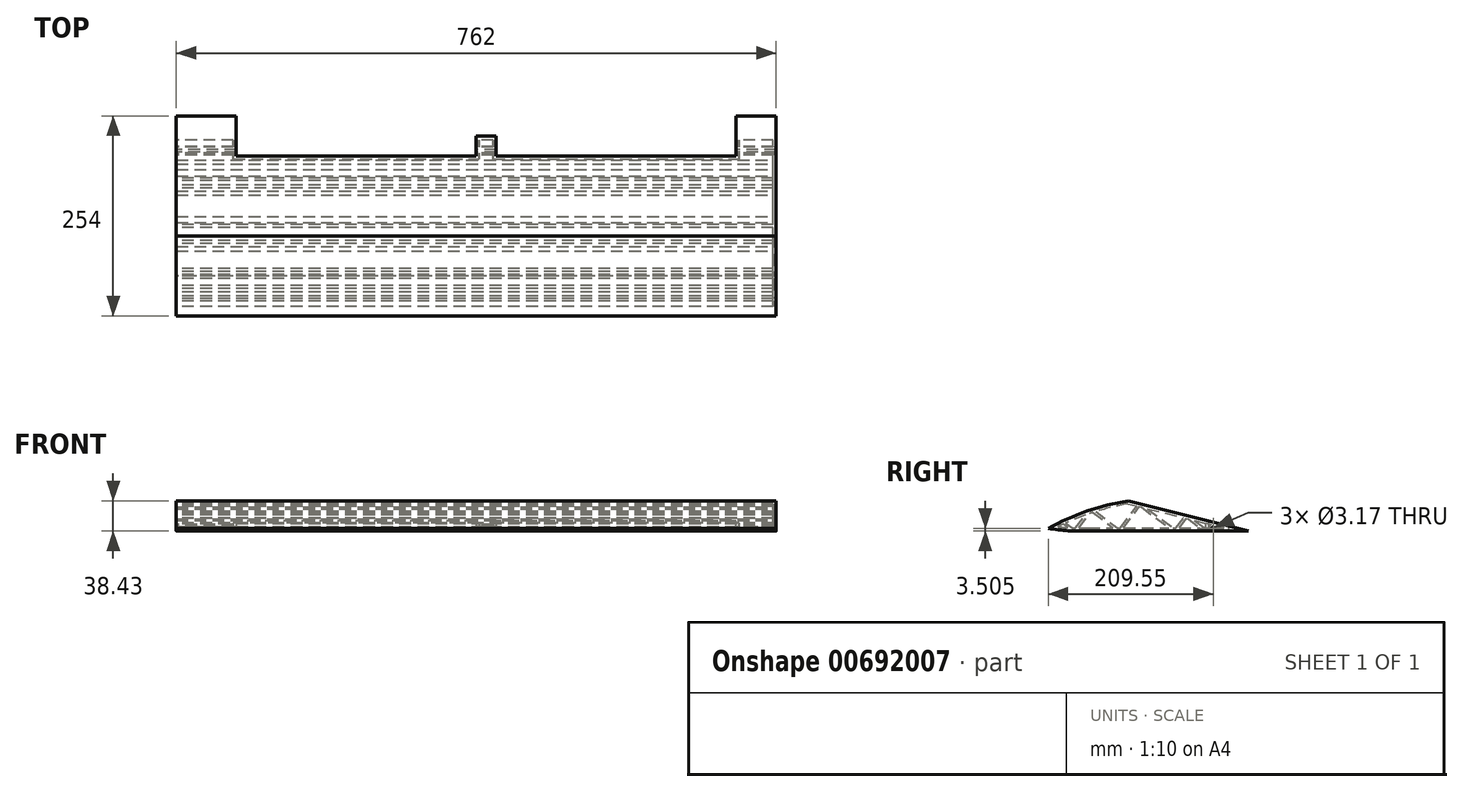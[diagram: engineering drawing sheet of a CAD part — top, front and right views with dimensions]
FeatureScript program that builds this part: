
annotation { "Feature Type Name" : "Feature", "Feature Type Description" : "" }
export const myFeature = defineFeature(function(context is Context, id is Id, definition is map)
    precondition{}
    {
        {
            var Q0;
            Q0=qCreatedBy(makeId("Right.planeOp"),FACE);
            var sketch = newSketch(context, id + "F0", { "sketchPlane" : qUnion([Q0])});
            skLineSegment(sketch, "E0.bottom", {"start": v(-127, 19.05) * mm, "end": v(127, 19.05) * mm});
            skLineSegment(sketch, "E0.top", {"start": v(-127, -19.05) * mm, "end": v(-120.65, -19.05) * mm});
            skLineSegment(sketch, "E0.left", {"start": v(-127, 19.05) * mm, "end": v(-127, -19.05) * mm});
            skLineSegment(sketch, "E0.right", {"start": v(127, 19.05) * mm, "end": v(127, -19.05) * mm});
            skPoint(sketch, "E0.middle", {"position": v(0, 0) * mm});
            skLineSegment(sketch, "E1", {"start": v(-123.83, -17.46) * mm, "end": v(-127, -15.88) * mm});
            skLineSegment(sketch, "E2", {"start": v(-127, 19.05) * mm, "end": v(-76.2, 19.05) * mm});
            skLineSegment(sketch, "E3", {"start": v(-76.2, 19.05) * mm, "end": v(-76.2, 6.35) * mm});
            skLineSegment(sketch, "E4", {"start": v(-127, 19.05) * mm, "end": v(-25.4, 19.05) * mm});
            skLineSegment(sketch, "E5", {"start": v(-25.4, 19.05) * mm, "end": v(127, -19.05) * mm});
            skLineSegment(sketch, "E6", {"start": v(-76.2, 6.35) * mm, "end": v(-76.2, -19.05) * mm});
            skArc(sketch, "E7", {"start": v(-127, -15.88) * mm, "mid": v(-101.7, -18.95) * mm, "end": v(-76.2, -19.05) * mm});
            skLineSegment(sketch, "E8.trimOffspring", {"start": v(-76.2, -19.05) * mm, "end": v(127, -19.05) * mm});
            skPoint(sketch, "E9.orphan", {"position": v(-123.83, -17.46) * mm});
            skPoint(sketch, "E10.orphan", {"position": v(-76.2, -17.46) * mm});
            skPoint(sketch, "E11.end.orphan", {"position": v(-100.01, -17.46) * mm});
            skArc(sketch, "E12", {"start": v(-25.4, 19.05) * mm, "mid": v(-77.67, 5.85) * mm, "end": v(-127, -15.88) * mm});
            skLineSegment(sketch, "E13", {"start": v(127, -19.05) * mm, "end": v(101.6, -19.05) * mm});
            skLineSegment(sketch, "E14", {"start": v(101.6, -19.05) * mm, "end": v(76.2, -19.05) * mm});
            skLineSegment(sketch, "E15", {"start": v(76.2, -19.05) * mm, "end": v(50.8, 0) * mm});
            skLineSegment(sketch, "E16", {"start": v(50.8, 0) * mm, "end": v(36.51, -19.05) * mm});
            skLineSegment(sketch, "E17", {"start": v(36.51, -19.05) * mm, "end": v(-8.73, 14.88) * mm});
            skLineSegment(sketch, "E18", {"start": v(-8.73, 14.88) * mm, "end": v(-34.18, -19.05) * mm});
            skLineSegment(sketch, "E19", {"start": v(-34.18, -19.05) * mm, "end": v(-70.53, 8.21) * mm});
            skLineSegment(sketch, "E20", {"start": v(-70.53, 8.21) * mm, "end": v(-91.2, -19.35) * mm});
            skLineSegment(sketch, "E21", {"start": v(-91.2, -19.35) * mm, "end": v(-108.35, -6.5) * mm});
            skLineSegment(sketch, "E22", {"start": v(76.2, -19.05) * mm, "end": v(74.3, -21.6) * mm});
            skLineSegment(sketch, "E23", {"start": v(74.3, -21.6) * mm, "end": v(48.9, -2.54) * mm});
            skLineSegment(sketch, "E24", {"start": v(48.9, -2.54) * mm, "end": v(46.36, -0.64) * mm});
            skLineSegment(sketch, "E25", {"start": v(46.36, -0.64) * mm, "end": v(33.97, -17.14) * mm});
            skLineSegment(sketch, "E26", {"start": v(33.97, -17.14) * mm, "end": v(32.07, -19.68) * mm});
            skLineSegment(sketch, "E27", {"start": v(32.07, -19.68) * mm, "end": v(-10.64, 12.34) * mm});
            skLineSegment(sketch, "E28", {"start": v(-10.64, 12.34) * mm, "end": v(-13.18, 14.25) * mm});
            skLineSegment(sketch, "E29", {"start": v(-13.18, 14.25) * mm, "end": v(-36.72, -17.14) * mm});
            skLineSegment(sketch, "E30", {"start": v(-36.72, -17.14) * mm, "end": v(-38.63, -19.68) * mm});
            skLineSegment(sketch, "E31", {"start": v(-38.63, -19.68) * mm, "end": v(-72.43, 5.67) * mm});
            skLineSegment(sketch, "E32", {"start": v(-72.43, 5.67) * mm, "end": v(-74.97, 7.58) * mm});
            skLineSegment(sketch, "E33", {"start": v(-74.97, 7.58) * mm, "end": v(-93.74, -17.45) * mm});
            skLineSegment(sketch, "E34", {"start": v(-93.74, -17.45) * mm, "end": v(-95.65, -19.99) * mm});
            skLineSegment(sketch, "E35", {"start": v(-95.65, -19.99) * mm, "end": v(-111.6, -8.02) * mm});
            skLineSegment(sketch, "E36", {"start": v(127, -19.05) * mm, "end": v(82.55, -19.05) * mm});
            skLineSegment(sketch, "E37", {"start": v(82.55, -19.05) * mm, "end": v(82.55, -15.88) * mm});
            skCircle(sketch, "E38", {"center": v(82.55, -15.88) * mm, "radius": 1.59 * mm});
            skSolve(sketch);
        }
        {
            var Q0;
            {var subQ0=sQuery(id+"F0.wireOp",EDGE,"E1");Q0=makeQuery(id+"F0.imprint","IMPRINT",FACE,{"disambiguationData":[TD([[makeQuery(id+"F0.imprint","IMPRINT",EDGE,{"derivedFrom":subQ0}),-1.0]])]});}
            var Q1;
            {var subQ0=sQuery(id+"F0.wireOp",EDGE,"E5");Q1=makeQuery(id+"F0.imprint","IMPRINT",FACE,{"disambiguationData":[TD([[makeQuery(id+"F0.imprint","IMPRINT",EDGE,{"derivedFrom":subQ0}),-1.0]])]});}
            var Q2;
            {var subQ0=sQuery(id+"F0.wireOp",EDGE,"E15");Q2=makeQuery(id+"F0.imprint","IMPRINT",FACE,{"disambiguationData":[TD([[makeQuery(id+"F0.imprint","IMPRINT",EDGE,{"derivedFrom":subQ0}),1.0]])]});}
            var Q3;
            {var subQ0=sQuery(id+"F0.wireOp",EDGE,"E23");var subQ1=sQuery(id+"F0.wireOp",EDGE,"E8.trimOffspring");var subQ2=makeQuery(id+"F0.imprint","INTERSECT",VERTEX,{"derivedFrom":[subQ1,subQ0]});Q3=makeQuery(id+"F0.imprint","IMPRINT",FACE,{"disambiguationData":[TD([[makeQuery(id+"F0.imprint","IMPRINT",EDGE,{"disambiguationData":[TD([[subQ2,1.0]])],"derivedFrom":subQ1}),1.0]])]});}
            var Q4;
            {var subQ0=sQuery(id+"F0.wireOp",EDGE,"E24");Q4=makeQuery(id+"F0.imprint","IMPRINT",FACE,{"disambiguationData":[TD([[makeQuery(id+"F0.imprint","IMPRINT",EDGE,{"derivedFrom":subQ0}),1.0]])]});}
            var Q5;
            {var subQ4=sQuery(id+"F0.wireOp",EDGE,"E24");Q5=makeQuery(id+"F0.imprint","IMPRINT",FACE,{"disambiguationData":[TD([[makeQuery(id+"F0.imprint","IMPRINT",EDGE,{"derivedFrom":subQ4}),-1.0]])]});}
            var Q6;
            {var subQ1=sQuery(id+"F0.wireOp",EDGE,"E8.trimOffspring");var subQ3=sQuery(id+"F0.wireOp",EDGE,"E27");var subQ4=makeQuery(id+"F0.imprint","INTERSECT",VERTEX,{"derivedFrom":[subQ1,subQ3]});Q6=makeQuery(id+"F0.imprint","IMPRINT",FACE,{"disambiguationData":[TD([[makeQuery(id+"F0.imprint","IMPRINT",EDGE,{"disambiguationData":[TD([[subQ4,1.0]])],"derivedFrom":subQ1}),1.0]])]});}
            var Q7;
            {var subQ8=sQuery(id+"F0.wireOp",EDGE,"E28");Q7=makeQuery(id+"F0.imprint","IMPRINT",FACE,{"disambiguationData":[TD([[makeQuery(id+"F0.imprint","IMPRINT",EDGE,{"derivedFrom":subQ8}),-1.0]])]});}
            var Q8;
            {var subQ0=sQuery(id+"F0.wireOp",EDGE,"E20");var subQ1=sQuery(id+"F0.wireOp",EDGE,"E6");var subQ2=makeQuery(id+"F0.imprint","INTERSECT",VERTEX,{"derivedFrom":[subQ1,subQ0]});Q8=makeQuery(id+"F0.imprint","IMPRINT",FACE,{"disambiguationData":[TD([[makeQuery(id+"F0.imprint","IMPRINT",EDGE,{"disambiguationData":[TD([[subQ2,-1.0]])],"derivedFrom":subQ1}),1.0]])]});}
            var Q9;
            {var subQ1=sQuery(id+"F0.wireOp",EDGE,"E6");var subQ3=sQuery(id+"F0.wireOp",EDGE,"E33");var subQ4=makeQuery(id+"F0.imprint","INTERSECT",VERTEX,{"derivedFrom":[subQ1,subQ3]});Q9=makeQuery(id+"F0.imprint","IMPRINT",FACE,{"disambiguationData":[TD([[makeQuery(id+"F0.imprint","IMPRINT",EDGE,{"disambiguationData":[TD([[subQ4,1.0]])],"derivedFrom":subQ1}),-1.0]])]});}
            var Q10;
            {var subQ3=sQuery(id+"F0.wireOp",EDGE,"E7");var subQ7=sQuery(id+"F0.wireOp",EDGE,"E35");var subQ9=makeQuery(id+"F0.imprint","INTERSECT",VERTEX,{"derivedFrom":[subQ3,subQ7]});Q10=makeQuery(id+"F0.imprint","IMPRINT",FACE,{"disambiguationData":[TD([[makeQuery(id+"F0.imprint","IMPRINT",EDGE,{"disambiguationData":[TD([[subQ9,-1.0]])],"derivedFrom":subQ3}),1.0]])]});}
            var Q11;
            {var subQ0=sQuery(id+"F0.wireOp",EDGE,"E20");var subQ1=sQuery(id+"F0.wireOp",EDGE,"E6");var subQ2=makeQuery(id+"F0.imprint","INTERSECT",VERTEX,{"derivedFrom":[subQ1,subQ0]});Q11=makeQuery(id+"F0.imprint","IMPRINT",FACE,{"disambiguationData":[TD([[makeQuery(id+"F0.imprint","IMPRINT",EDGE,{"disambiguationData":[TD([[subQ2,1.0]])],"derivedFrom":subQ1}),-1.0]])]});}
            var Q12;
            {var subQ0=sQuery(id+"F0.wireOp",EDGE,"E30");var subQ1=sQuery(id+"F0.wireOp",EDGE,"E8.trimOffspring");var subQ2=makeQuery(id+"F0.imprint","INTERSECT",VERTEX,{"derivedFrom":[subQ1,subQ0]});Q12=makeQuery(id+"F0.imprint","IMPRINT",FACE,{"disambiguationData":[TD([[makeQuery(id+"F0.imprint","IMPRINT",EDGE,{"disambiguationData":[TD([[subQ2,1.0]])],"derivedFrom":subQ1}),1.0]])]});}
            var Q13;
            {var subQ1=sQuery(id+"F0.wireOp",EDGE,"E20");var subQ5=sQuery(id+"F0.wireOp",EDGE,"E6");var subQ6=makeQuery(id+"F0.imprint","INTERSECT",VERTEX,{"derivedFrom":[subQ5,subQ1]});Q13=makeQuery(id+"F0.imprint","IMPRINT",FACE,{"disambiguationData":[TD([[makeQuery(id+"F0.imprint","IMPRINT",EDGE,{"disambiguationData":[TD([[subQ6,1.0]])],"derivedFrom":subQ5}),1.0]])]});}
            var Q14;
            {var subQ3=sQuery(id+"F0.wireOp",EDGE,"E28");Q14=makeQuery(id+"F0.imprint","IMPRINT",FACE,{"disambiguationData":[TD([[makeQuery(id+"F0.imprint","IMPRINT",EDGE,{"derivedFrom":subQ3}),1.0]])]});}
            var Q15;
            {var subQ3=sQuery(id+"F0.wireOp",EDGE,"E8.trimOffspring");var subQ7=sQuery(id+"F0.wireOp",EDGE,"E27");var subQ9=makeQuery(id+"F0.imprint","INTERSECT",VERTEX,{"derivedFrom":[subQ3,subQ7]});Q15=makeQuery(id+"F0.imprint","IMPRINT",FACE,{"disambiguationData":[TD([[makeQuery(id+"F0.imprint","IMPRINT",EDGE,{"disambiguationData":[TD([[subQ9,-1.0]])],"derivedFrom":subQ3}),1.0]])]});}
            var Q16;
            {var subQ1=sQuery(id+"F0.wireOp",EDGE,"E8.trimOffspring");var subQ3=sQuery(id+"F0.wireOp",EDGE,"E26");var subQ4=makeQuery(id+"F0.imprint","INTERSECT",VERTEX,{"derivedFrom":[subQ1,subQ3]});Q16=makeQuery(id+"F0.imprint","IMPRINT",FACE,{"disambiguationData":[TD([[makeQuery(id+"F0.imprint","IMPRINT",EDGE,{"disambiguationData":[TD([[subQ4,-1.0]])],"derivedFrom":subQ1}),1.0]])]});}
            var Q17;
            {var subQ1=sQuery(id+"F0.wireOp",EDGE,"E8.trimOffspring");var subQ3=sQuery(id+"F0.wireOp",EDGE,"E30");var subQ4=makeQuery(id+"F0.imprint","INTERSECT",VERTEX,{"derivedFrom":[subQ1,subQ3]});Q17=makeQuery(id+"F0.imprint","IMPRINT",FACE,{"disambiguationData":[TD([[makeQuery(id+"F0.imprint","IMPRINT",EDGE,{"disambiguationData":[TD([[subQ4,-1.0]])],"derivedFrom":subQ1}),1.0]])]});}
            var Q18;
            {var subQ0=sQuery(id+"F0.wireOp",EDGE,"E34");var subQ1=sQuery(id+"F0.wireOp",EDGE,"E7");var subQ2=makeQuery(id+"F0.imprint","INTERSECT",VERTEX,{"derivedFrom":[subQ1,subQ0]});Q18=makeQuery(id+"F0.imprint","IMPRINT",FACE,{"disambiguationData":[TD([[makeQuery(id+"F0.imprint","IMPRINT",EDGE,{"disambiguationData":[TD([[subQ2,-1.0]])],"derivedFrom":subQ1}),1.0]])]});}
            var Q19;
            {var subQ0=sQuery(id+"F0.wireOp",EDGE,"E20");var subQ1=sQuery(id+"F0.wireOp",EDGE,"E6");var subQ2=makeQuery(id+"F0.imprint","INTERSECT",VERTEX,{"derivedFrom":[subQ1,subQ0]});Q19=makeQuery(id+"F0.imprint","IMPRINT",FACE,{"disambiguationData":[TD([[makeQuery(id+"F0.imprint","IMPRINT",EDGE,{"disambiguationData":[TD([[subQ2,-1.0]])],"derivedFrom":subQ1}),-1.0]])]});}
            var Q20;
            {var subQ1=sQuery(id+"F0.wireOp",EDGE,"E12");var subQ3=sQuery(id+"F0.wireOp",EDGE,"E32");var subQ4=makeQuery(id+"F0.imprint","INTERSECT",VERTEX,{"derivedFrom":[subQ1,subQ3]});Q20=makeQuery(id+"F0.imprint","IMPRINT",FACE,{"disambiguationData":[TD([[makeQuery(id+"F0.imprint","IMPRINT",EDGE,{"disambiguationData":[TD([[subQ4,1.0]])],"derivedFrom":subQ1}),1.0]])]});}
            var Q21;
            {var subQ1=sQuery(id+"F0.wireOp",EDGE,"E6");var subQ3=sQuery(id+"F0.wireOp",EDGE,"E33");var subQ4=makeQuery(id+"F0.imprint","INTERSECT",VERTEX,{"derivedFrom":[subQ1,subQ3]});Q21=makeQuery(id+"F0.imprint","IMPRINT",FACE,{"disambiguationData":[TD([[makeQuery(id+"F0.imprint","IMPRINT",EDGE,{"disambiguationData":[TD([[subQ4,1.0]])],"derivedFrom":subQ3}),-1.0]])]});}
            var Q22;
            {var subQ1=sQuery(id+"F0.wireOp",EDGE,"E7");var subQ3=sQuery(id+"F0.wireOp",EDGE,"E35");var subQ4=makeQuery(id+"F0.imprint","INTERSECT",VERTEX,{"derivedFrom":[subQ1,subQ3]});Q22=makeQuery(id+"F0.imprint","IMPRINT",FACE,{"disambiguationData":[TD([[makeQuery(id+"F0.imprint","IMPRINT",EDGE,{"disambiguationData":[TD([[subQ4,-1.0]])],"derivedFrom":subQ3}),1.0]])]});}
            extrude(context, id + "F1", {"entities" : qUnion([Q0, Q1, Q2, Q3, Q4, Q5, Q6, Q7, Q8, Q9, Q10, Q11, Q12, Q13, Q14, Q15, Q16, Q17, Q18, Q19, Q20, Q21, Q22]), "depth" : 762 * mm, "offsetDistance" : 25.4 * mm});
        }
        {
            var Q0;
            Q0=makeQuery(id+"F1.opExtrude","SWEPT_BODY",BODY,{"disambiguationData":[OSD([sQuery(id+"F0.wireOp",EDGE,"E0.top"),sQuery(id+"F0.wireOp",EDGE,"E1"),sQuery(id+"F0.wireOp",EDGE,"54O46Pbj-JXbp-sWDO-WlFE-3hnwlmeF4VM1"),sQuery(id+"F0.wireOp",EDGE,"I7tgXKDc-7YU1-26Oo-DtxB-X4BbDVzCFCnU"),sQuery(id+"F0.wireOp",EDGE,"E5")])]});
            var Q1;
            Q1=qCreatedBy(makeId("Right.planeOp"),FACE);
            mirror(context, id + "F2", {"operationType" : NewBodyOperationType.ADD, "entities" : qUnion([Q0]), "mirrorPlane" : qUnion([Q1])});
        }
        {
            var Q0;
            {var subQ0=sQuery(id+"F0.wireOp",EDGE,"E15");Q0=makeQuery(id+"F0.imprint","IMPRINT",FACE,{"disambiguationData":[TD([[makeQuery(id+"F0.imprint","IMPRINT",EDGE,{"derivedFrom":subQ0}),1.0]])]});}
            var Q1;
            {var subQ0=sQuery(id+"F0.wireOp",EDGE,"E24");Q1=makeQuery(id+"F0.imprint","IMPRINT",FACE,{"disambiguationData":[TD([[makeQuery(id+"F0.imprint","IMPRINT",EDGE,{"derivedFrom":subQ0}),1.0]])]});}
            var Q2;
            {var subQ3=sQuery(id+"F0.wireOp",EDGE,"E8.trimOffspring");var subQ7=sQuery(id+"F0.wireOp",EDGE,"E27");var subQ9=makeQuery(id+"F0.imprint","INTERSECT",VERTEX,{"derivedFrom":[subQ3,subQ7]});Q2=makeQuery(id+"F0.imprint","IMPRINT",FACE,{"disambiguationData":[TD([[makeQuery(id+"F0.imprint","IMPRINT",EDGE,{"disambiguationData":[TD([[subQ9,-1.0]])],"derivedFrom":subQ3}),1.0]])]});}
            var Q3;
            {var subQ3=sQuery(id+"F0.wireOp",EDGE,"E28");Q3=makeQuery(id+"F0.imprint","IMPRINT",FACE,{"disambiguationData":[TD([[makeQuery(id+"F0.imprint","IMPRINT",EDGE,{"derivedFrom":subQ3}),1.0]])]});}
            var Q4;
            {var subQ0=sQuery(id+"F0.wireOp",EDGE,"E30");var subQ1=sQuery(id+"F0.wireOp",EDGE,"E8.trimOffspring");var subQ2=makeQuery(id+"F0.imprint","INTERSECT",VERTEX,{"derivedFrom":[subQ1,subQ0]});Q4=makeQuery(id+"F0.imprint","IMPRINT",FACE,{"disambiguationData":[TD([[makeQuery(id+"F0.imprint","IMPRINT",EDGE,{"disambiguationData":[TD([[subQ2,1.0]])],"derivedFrom":subQ1}),1.0]])]});}
            var Q5;
            {var subQ0=sQuery(id+"F0.wireOp",EDGE,"E20");var subQ1=sQuery(id+"F0.wireOp",EDGE,"E6");var subQ2=makeQuery(id+"F0.imprint","INTERSECT",VERTEX,{"derivedFrom":[subQ1,subQ0]});Q5=makeQuery(id+"F0.imprint","IMPRINT",FACE,{"disambiguationData":[TD([[makeQuery(id+"F0.imprint","IMPRINT",EDGE,{"disambiguationData":[TD([[subQ2,1.0]])],"derivedFrom":subQ1}),-1.0]])]});}
            var Q6;
            {var subQ3=sQuery(id+"F0.wireOp",EDGE,"E7");var subQ7=sQuery(id+"F0.wireOp",EDGE,"E35");var subQ9=makeQuery(id+"F0.imprint","INTERSECT",VERTEX,{"derivedFrom":[subQ3,subQ7]});Q6=makeQuery(id+"F0.imprint","IMPRINT",FACE,{"disambiguationData":[TD([[makeQuery(id+"F0.imprint","IMPRINT",EDGE,{"disambiguationData":[TD([[subQ9,-1.0]])],"derivedFrom":subQ3}),1.0]])]});}
            var Q7;
            {var subQ1=sQuery(id+"F0.wireOp",EDGE,"E20");var subQ5=sQuery(id+"F0.wireOp",EDGE,"E6");var subQ6=makeQuery(id+"F0.imprint","INTERSECT",VERTEX,{"derivedFrom":[subQ5,subQ1]});Q7=makeQuery(id+"F0.imprint","IMPRINT",FACE,{"disambiguationData":[TD([[makeQuery(id+"F0.imprint","IMPRINT",EDGE,{"disambiguationData":[TD([[subQ6,1.0]])],"derivedFrom":subQ5}),1.0]])]});}
            extrude(context, id + "F3", {"entities" : qUnion([Q0, Q1, Q2, Q3, Q4, Q5, Q6, Q7]), "operationType" : NewBodyOperationType.ADD, "depth" : 762 * mm, "offsetDistance" : 25.4 * mm});
        }
        {
            var Q0;
            {var subQ0=makeQuery(id+"F1.opExtrude","SWEPT_FACE",FACE,{"disambiguationData":[OSD([sQuery(id+"F0.wireOp",EDGE,"E8.trimOffspring")])]});Q0=makeQuery(id+"F2.boolean.opBoolean","MERGE",FACE,{"derivedFrom":[subQ0,makeQuery(id+"F2.opPattern","COPY",FACE,{"derivedFrom":subQ0,"instanceName":"1"})]});}
            var sketch = newSketch(context, id + "F4", { "sketchPlane" : qUnion([Q0])});
            skLineSegment(sketch, "E39", {"start": v(0, -127) * mm, "end": v(0, 312.49) * mm});
            skLineSegment(sketch, "E40", {"start": v(0, 312.49) * mm, "end": v(931.06, 312.49) * mm});
            skLineSegment(sketch, "E41", {"start": v(931.06, 312.49) * mm, "end": v(931.06, -488.96) * mm});
            skLineSegment(sketch, "E42", {"start": v(931.06, -488.96) * mm, "end": v(0, -488.96) * mm});
            skLineSegment(sketch, "E43", {"start": v(0, -488.96) * mm, "end": v(0, 0) * mm});
            skSolve(sketch);
        }
        {
            var Q0;
            {var subQ0=sQuery(id+"F0.wireOp",EDGE,"E8.trimOffspring");var subQ3=makeQuery(id+"F2.opPattern","COPY",EDGE,{"derivedFrom":makeQuery(id+"F1.opExtrude","CAP_EDGE",EDGE,{"disambiguationData":[OSD([subQ0])],"isStart":false}),"instanceName":"1"});Q0=makeQuery(id+"F4.imprint","IMPRINT",FACE,{"disambiguationData":[TD([[makeQuery(id+"F4.imprint","IMPRINT",EDGE,{"derivedFrom":subQ3}),1.0]])]});}
            var sketch = newSketch(context, id + "F5", { "sketchPlane" : qUnion([Q0])});
            skLineSegment(sketch, "E44", {"start": v(0, 0) * mm, "end": v(0, -127) * mm});
            skLineSegment(sketch, "E45", {"start": v(0, -127) * mm, "end": v(0, -50.8) * mm});
            skLineSegment(sketch, "E46", {"start": v(0, -50.8) * mm, "end": v(0, -127) * mm});
            skLineSegment(sketch, "E47", {"start": v(0, -127) * mm, "end": v(-76.2, -127) * mm});
            skLineSegment(sketch, "E48", {"start": v(-76.2, -127) * mm, "end": v(-76.2, -76.2) * mm});
            skLineSegment(sketch, "E49", {"start": v(-76.2, -76.2) * mm, "end": v(-711.2, -76.2) * mm});
            skLineSegment(sketch, "E50", {"start": v(-711.2, -76.2) * mm, "end": v(-711.2, -127) * mm});
            skLineSegment(sketch, "E51.bottom", {"start": v(-381, -50.8) * mm, "end": v(-406.4, -50.8) * mm});
            skLineSegment(sketch, "E51.top", {"start": v(-381, -101.6) * mm, "end": v(-406.4, -101.6) * mm});
            skLineSegment(sketch, "E51.left", {"start": v(-381, -50.8) * mm, "end": v(-381, -101.6) * mm});
            skLineSegment(sketch, "E51.right", {"start": v(-406.4, -50.8) * mm, "end": v(-406.4, -101.6) * mm});
            skPoint(sketch, "E51.middle", {"position": v(-393.7, -76.2) * mm});
            skSolve(sketch);
        }
        {
            var Q0;
            {var subQ0=sQuery(id+"F5.wireOp",EDGE,"E48");Q0=makeQuery(id+"F5.imprint","IMPRINT",FACE,{"disambiguationData":[TD([[makeQuery(id+"F5.imprint","IMPRINT",EDGE,{"derivedFrom":subQ0}),1.0]])]});}
            extrude(context, id + "F6", {"entities" : qUnion([Q0]), "operationType" : NewBodyOperationType.REMOVE, "oppositeDirection" : true, "depth" : 25.4 * mm, "offsetDistance" : 25.4 * mm});
        }
        {
            var Q0;
            {var subQ0=makeQuery(id+"F1.opExtrude","SWEPT_FACE",FACE,{"disambiguationData":[OSD([sQuery(id+"F0.wireOp",EDGE,"E8.trimOffspring")])]});Q0=makeQuery(id+"F2.boolean.opBoolean","MERGE",FACE,{"derivedFrom":[subQ0,makeQuery(id+"F2.opPattern","COPY",FACE,{"derivedFrom":subQ0,"instanceName":"1"})]});}
            var sketch = newSketch(context, id + "F7", { "sketchPlane" : qUnion([Q0])});
            skLineSegment(sketch, "E52", {"start": v(0, 0) * mm, "end": v(0, -127) * mm});
            skLineSegment(sketch, "E53", {"start": v(0, -127) * mm, "end": v(76.2, -127) * mm});
            skLineSegment(sketch, "E54", {"start": v(76.2, -127) * mm, "end": v(76.2, -76.2) * mm});
            skLineSegment(sketch, "E55", {"start": v(76.2, -76.2) * mm, "end": v(711.2, -76.2) * mm});
            skLineSegment(sketch, "E56", {"start": v(711.2, -76.2) * mm, "end": v(711.2, -127) * mm});
            skLineSegment(sketch, "E57.bottom", {"start": v(406.4, -101.6) * mm, "end": v(381, -101.6) * mm});
            skLineSegment(sketch, "E57.top", {"start": v(406.4, -50.8) * mm, "end": v(381, -50.8) * mm});
            skLineSegment(sketch, "E57.left", {"start": v(406.4, -101.6) * mm, "end": v(406.4, -50.8) * mm});
            skLineSegment(sketch, "E57.right", {"start": v(381, -101.6) * mm, "end": v(381, -50.8) * mm});
            skPoint(sketch, "E57.middle", {"position": v(393.7, -76.2) * mm});
            skSolve(sketch);
        }
        {
            var Q0;
            {var subQ1=sQuery(id+"F7.wireOp",EDGE,"E54");Q0=makeQuery(id+"F7.imprint","IMPRINT",FACE,{"disambiguationData":[TD([[makeQuery(id+"F7.imprint","IMPRINT",EDGE,{"derivedFrom":subQ1}),-1.0]])]});}
            extrude(context, id + "F8", {"entities" : qUnion([Q0]), "operationType" : NewBodyOperationType.REMOVE, "endBound" : BoundingType.THROUGH_ALL, "oppositeDirection" : true, "depth" : 25.4 * mm, "offsetDistance" : 25.4 * mm});
        }
        {
            var Q0;
            Q0=makeQuery(id+"F2.opPattern","COPY",FACE,{"derivedFrom":makeQuery(id+"F1.opExtrude","CAP_FACE",FACE,{"disambiguationData":[OSD([sQuery(id+"F0.wireOp",EDGE,"E5"),sQuery(id+"F0.wireOp",EDGE,"E7"),sQuery(id+"F0.wireOp",EDGE,"E8.trimOffspring"),sQuery(id+"F0.wireOp",EDGE,"E12"),sQuery(id+"F0.wireOp",EDGE,"E38")])],"isStart":false}),"instanceName":"1"});
            shell(context, id + "F9", {"entities" : qUnion([Q0]), "thickness" : 3.8 * mm});
        }
        {
            var Q0;
            {var subQ0=sQuery(id+"F0.wireOp",EDGE,"E20");var subQ1=sQuery(id+"F0.wireOp",EDGE,"E6");var subQ2=makeQuery(id+"F0.imprint","INTERSECT",VERTEX,{"derivedFrom":[subQ1,subQ0]});Q0=makeQuery(id+"F0.imprint","IMPRINT",FACE,{"disambiguationData":[TD([[makeQuery(id+"F0.imprint","IMPRINT",EDGE,{"disambiguationData":[TD([[subQ2,1.0]])],"derivedFrom":subQ1}),-1.0]])]});}
            var Q1;
            {var subQ3=sQuery(id+"F0.wireOp",EDGE,"E7");var subQ7=sQuery(id+"F0.wireOp",EDGE,"E35");var subQ9=makeQuery(id+"F0.imprint","INTERSECT",VERTEX,{"derivedFrom":[subQ3,subQ7]});Q1=makeQuery(id+"F0.imprint","IMPRINT",FACE,{"disambiguationData":[TD([[makeQuery(id+"F0.imprint","IMPRINT",EDGE,{"disambiguationData":[TD([[subQ9,-1.0]])],"derivedFrom":subQ3}),1.0]])]});}
            var Q2;
            {var subQ1=sQuery(id+"F0.wireOp",EDGE,"E20");var subQ5=sQuery(id+"F0.wireOp",EDGE,"E6");var subQ6=makeQuery(id+"F0.imprint","INTERSECT",VERTEX,{"derivedFrom":[subQ5,subQ1]});Q2=makeQuery(id+"F0.imprint","IMPRINT",FACE,{"disambiguationData":[TD([[makeQuery(id+"F0.imprint","IMPRINT",EDGE,{"disambiguationData":[TD([[subQ6,1.0]])],"derivedFrom":subQ5}),1.0]])]});}
            var Q3;
            {var subQ0=sQuery(id+"F0.wireOp",EDGE,"E30");var subQ1=sQuery(id+"F0.wireOp",EDGE,"E8.trimOffspring");var subQ2=makeQuery(id+"F0.imprint","INTERSECT",VERTEX,{"derivedFrom":[subQ1,subQ0]});Q3=makeQuery(id+"F0.imprint","IMPRINT",FACE,{"disambiguationData":[TD([[makeQuery(id+"F0.imprint","IMPRINT",EDGE,{"disambiguationData":[TD([[subQ2,1.0]])],"derivedFrom":subQ1}),1.0]])]});}
            var Q4;
            {var subQ3=sQuery(id+"F0.wireOp",EDGE,"E28");Q4=makeQuery(id+"F0.imprint","IMPRINT",FACE,{"disambiguationData":[TD([[makeQuery(id+"F0.imprint","IMPRINT",EDGE,{"derivedFrom":subQ3}),1.0]])]});}
            var Q5;
            {var subQ3=sQuery(id+"F0.wireOp",EDGE,"E8.trimOffspring");var subQ7=sQuery(id+"F0.wireOp",EDGE,"E27");var subQ9=makeQuery(id+"F0.imprint","INTERSECT",VERTEX,{"derivedFrom":[subQ3,subQ7]});Q5=makeQuery(id+"F0.imprint","IMPRINT",FACE,{"disambiguationData":[TD([[makeQuery(id+"F0.imprint","IMPRINT",EDGE,{"disambiguationData":[TD([[subQ9,-1.0]])],"derivedFrom":subQ3}),1.0]])]});}
            var Q6;
            {var subQ0=sQuery(id+"F0.wireOp",EDGE,"E24");Q6=makeQuery(id+"F0.imprint","IMPRINT",FACE,{"disambiguationData":[TD([[makeQuery(id+"F0.imprint","IMPRINT",EDGE,{"derivedFrom":subQ0}),1.0]])]});}
            var Q7;
            {var subQ0=sQuery(id+"F0.wireOp",EDGE,"E15");Q7=makeQuery(id+"F0.imprint","IMPRINT",FACE,{"disambiguationData":[TD([[makeQuery(id+"F0.imprint","IMPRINT",EDGE,{"derivedFrom":subQ0}),1.0]])]});}
            extrude(context, id + "F10", {"entities" : qUnion([Q0, Q1, Q2, Q3, Q4, Q5, Q6, Q7]), "operationType" : NewBodyOperationType.ADD, "oppositeDirection" : true, "depth" : 762 * mm, "offsetDistance" : 25.4 * mm});
        }
        {
            var Q0;
            {var subQ0=sQuery(id+"F0.wireOp",EDGE,"E8.trimOffspring");var subQ3=makeQuery(id+"F2.opPattern","COPY",EDGE,{"derivedFrom":makeQuery(id+"F1.opExtrude","CAP_EDGE",EDGE,{"disambiguationData":[OSD([subQ0])],"isStart":false}),"instanceName":"1"});Q0=makeQuery(id+"F4.imprint","IMPRINT",FACE,{"disambiguationData":[TD([[makeQuery(id+"F4.imprint","IMPRINT",EDGE,{"derivedFrom":subQ3}),1.0]])]});}
            var sketch = newSketch(context, id + "F11", { "sketchPlane" : qUnion([Q0])});
            skLineSegment(sketch, "E58", {"start": v(0, 0) * mm, "end": v(0, 246.92) * mm});
            skLineSegment(sketch, "E59", {"start": v(0, 246.92) * mm, "end": v(-873.16, 246.92) * mm});
            skLineSegment(sketch, "E60", {"start": v(-873.16, 246.92) * mm, "end": v(-873.16, -331.46) * mm});
            skLineSegment(sketch, "E61", {"start": v(-873.16, -331.46) * mm, "end": v(0, -331.46) * mm});
            skLineSegment(sketch, "E62", {"start": v(0, -331.46) * mm, "end": v(0, 0) * mm});
            skSolve(sketch);
        }
        {
            var Q0;
            Q0 = qSketchRegion(id + "F11", true);
            extrude(context, id + "F12", {"entities" : qUnion([Q0]), "operationType" : NewBodyOperationType.REMOVE, "endBound" : BoundingType.THROUGH_ALL, "oppositeDirection" : true, "depth" : 25.4 * mm, "offsetDistance" : 25.4 * mm});
        }
        {
            var Q0;
            Q0 = qSketchRegion(id + "F11", true);
            extrude(context, id + "F13", {"entities" : qUnion([Q0]), "operationType" : NewBodyOperationType.REMOVE, "depth" : 25.4 * mm, "offsetDistance" : 25.4 * mm});
        }
        {
            var Q0;
            {var subQ0=sQuery(id+"F0.wireOp",EDGE,"E34");var subQ1=sQuery(id+"F0.wireOp",EDGE,"E7");var subQ2=makeQuery(id+"F0.imprint","INTERSECT",VERTEX,{"derivedFrom":[subQ1,subQ0]});Q0=makeQuery(id+"F0.imprint","IMPRINT",FACE,{"disambiguationData":[TD([[makeQuery(id+"F0.imprint","IMPRINT",EDGE,{"disambiguationData":[TD([[subQ2,-1.0]])],"derivedFrom":subQ1}),1.0]])]});}
            var Q1;
            {var subQ1=sQuery(id+"F0.wireOp",EDGE,"E8.trimOffspring");var subQ3=sQuery(id+"F0.wireOp",EDGE,"E30");var subQ4=makeQuery(id+"F0.imprint","INTERSECT",VERTEX,{"derivedFrom":[subQ1,subQ3]});Q1=makeQuery(id+"F0.imprint","IMPRINT",FACE,{"disambiguationData":[TD([[makeQuery(id+"F0.imprint","IMPRINT",EDGE,{"disambiguationData":[TD([[subQ4,-1.0]])],"derivedFrom":subQ1}),1.0]])]});}
            var Q2;
            {var subQ1=sQuery(id+"F0.wireOp",EDGE,"E8.trimOffspring");var subQ3=sQuery(id+"F0.wireOp",EDGE,"E26");var subQ4=makeQuery(id+"F0.imprint","INTERSECT",VERTEX,{"derivedFrom":[subQ1,subQ3]});Q2=makeQuery(id+"F0.imprint","IMPRINT",FACE,{"disambiguationData":[TD([[makeQuery(id+"F0.imprint","IMPRINT",EDGE,{"disambiguationData":[TD([[subQ4,-1.0]])],"derivedFrom":subQ1}),1.0]])]});}
            var Q3;
            {var subQ0=sQuery(id+"F0.wireOp",EDGE,"E24");Q3=makeQuery(id+"F0.imprint","IMPRINT",FACE,{"disambiguationData":[TD([[makeQuery(id+"F0.imprint","IMPRINT",EDGE,{"derivedFrom":subQ0}),1.0]])]});}
            var Q4;
            {var subQ3=sQuery(id+"F0.wireOp",EDGE,"E28");Q4=makeQuery(id+"F0.imprint","IMPRINT",FACE,{"disambiguationData":[TD([[makeQuery(id+"F0.imprint","IMPRINT",EDGE,{"derivedFrom":subQ3}),1.0]])]});}
            var Q5;
            {var subQ0=sQuery(id+"F0.wireOp",EDGE,"E20");var subQ1=sQuery(id+"F0.wireOp",EDGE,"E6");var subQ2=makeQuery(id+"F0.imprint","INTERSECT",VERTEX,{"derivedFrom":[subQ1,subQ0]});Q5=makeQuery(id+"F0.imprint","IMPRINT",FACE,{"disambiguationData":[TD([[makeQuery(id+"F0.imprint","IMPRINT",EDGE,{"disambiguationData":[TD([[subQ2,1.0]])],"derivedFrom":subQ1}),-1.0]])]});}
            var Q6;
            {var subQ0=sQuery(id+"F0.wireOp",EDGE,"E15");Q6=makeQuery(id+"F0.imprint","IMPRINT",FACE,{"disambiguationData":[TD([[makeQuery(id+"F0.imprint","IMPRINT",EDGE,{"derivedFrom":subQ0}),1.0]])]});}
            var Q7;
            {var subQ3=sQuery(id+"F0.wireOp",EDGE,"E7");var subQ7=sQuery(id+"F0.wireOp",EDGE,"E35");var subQ9=makeQuery(id+"F0.imprint","INTERSECT",VERTEX,{"derivedFrom":[subQ3,subQ7]});Q7=makeQuery(id+"F0.imprint","IMPRINT",FACE,{"disambiguationData":[TD([[makeQuery(id+"F0.imprint","IMPRINT",EDGE,{"disambiguationData":[TD([[subQ9,-1.0]])],"derivedFrom":subQ3}),1.0]])]});}
            var Q8;
            {var subQ3=sQuery(id+"F0.wireOp",EDGE,"E8.trimOffspring");var subQ7=sQuery(id+"F0.wireOp",EDGE,"E27");var subQ9=makeQuery(id+"F0.imprint","INTERSECT",VERTEX,{"derivedFrom":[subQ3,subQ7]});Q8=makeQuery(id+"F0.imprint","IMPRINT",FACE,{"disambiguationData":[TD([[makeQuery(id+"F0.imprint","IMPRINT",EDGE,{"disambiguationData":[TD([[subQ9,-1.0]])],"derivedFrom":subQ3}),1.0]])]});}
            var Q9;
            {var subQ0=sQuery(id+"F0.wireOp",EDGE,"E30");var subQ1=sQuery(id+"F0.wireOp",EDGE,"E8.trimOffspring");var subQ2=makeQuery(id+"F0.imprint","INTERSECT",VERTEX,{"derivedFrom":[subQ1,subQ0]});Q9=makeQuery(id+"F0.imprint","IMPRINT",FACE,{"disambiguationData":[TD([[makeQuery(id+"F0.imprint","IMPRINT",EDGE,{"disambiguationData":[TD([[subQ2,1.0]])],"derivedFrom":subQ1}),1.0]])]});}
            var Q10;
            {var subQ1=sQuery(id+"F0.wireOp",EDGE,"E20");var subQ5=sQuery(id+"F0.wireOp",EDGE,"E6");var subQ6=makeQuery(id+"F0.imprint","INTERSECT",VERTEX,{"derivedFrom":[subQ5,subQ1]});Q10=makeQuery(id+"F0.imprint","IMPRINT",FACE,{"disambiguationData":[TD([[makeQuery(id+"F0.imprint","IMPRINT",EDGE,{"disambiguationData":[TD([[subQ6,1.0]])],"derivedFrom":subQ5}),1.0]])]});}
            extrude(context, id + "F14", {"entities" : qUnion([Q0, Q1, Q2, Q3, Q4, Q5, Q6, Q7, Q8, Q9, Q10]), "operationType" : NewBodyOperationType.ADD, "depth" : 762 * mm, "offsetDistance" : 25.4 * mm});
        }
    });
